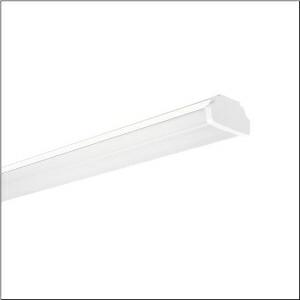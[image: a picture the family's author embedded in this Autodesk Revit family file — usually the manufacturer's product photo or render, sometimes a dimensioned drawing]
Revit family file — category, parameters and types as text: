
# Revit family: modario_r__31_ho_53bm811m1v4120_5d14
name_source: partatom
category: Lighting Fixtures
units: mm (PartAtom-declared; Revit-internal decimal feet)

## family parameters
Cut with Voids When Loaded = No
Host = Face
Light Source = No
Part Type = Normal
Room Calculation Point = No
Round Connector Dimension = Use Diameter
Shared = No

## types (1)
- --- (1 x LED, 12380 lm, 77.3 W, 4000K)
    Apparent Load = 77 VA
    CIE Flux Codes = 52 78 94 90 100
    Color Rendering = 80
    Color Temperature = 4000K
    Default Elevation = 1800 mm
    Description = Modario® 31 HO, luminaire insert, of sheet steel, coil coated, white, length: 1.495mm, width: 81mm, height: 82mm, LED rated luminous flux: 12.380lm, light colour: 840, control gear: ON/OFF Multilumen, control gear: ECG Multilumen, with plug, 3-pole, with phase selection, mains connection: 220..240V, AC, 50/60Hz, primary optical cover: cover, of PMMA, light emission: direct distribution, primary light characteristic: symmetric, protection rating (complete): IP20, protection rating (LED compartment): IP50, insulation class (complete): insulation class I (protective earthing), certification: CE, ENEC, VDE, UKCA, permissible ambient temperature for indoor applications: -35..+35°C, corresponds to IFS (International Featured Standards) requirements for safety and quality in the food industry, reducing of maximum allowable ambient temperature of 5°C with ceiling mounting, packaging unit: 1 piece
    Height = 92 mm
    Lamp = 1 x LED
    Lamp Light Flux = 12380 lm
    Lamp Power = 77.3 W
    Lamp count = 1
    Length = 1495 mm
    Luminous efficacy = 160 lm/W
    Manufacturer = Siteco
    ModVariant = No
    Model = 53BM811M1V4120
    Mounting Place = Ceiling
    Mounting Type = Pendant
    Number of Poles = 1
    OnlyDefault = Yes
    Power Factor = 1
    Product Name = Modario® 31 HO
    Product group = luminaire insert
    ProductGroupID = 902
    Protection Class = Protection class I
    Protection Degree = IP 20
    RLX_Detail_Level = 1
    RlxData = <blob elided: 40045 chars, md5=07634e21>
    Socket = socket
    Standby Power = 0 W
    System Light Flux = 12380 lm
    System Power = 77 W
    Type Comments = factory setting: luminous flux: 100 % | (A | C | E) | 173 mA
    Type Image = l_1003447.jpg
    URL = http://relux.com
    VarID = @adj_125385
    Voltage = 0 V
    Weight = 0.00 kg
    Width = 81 mm

## geometry (parser evidence)
native form markers: Blend x4, Sweep x11
no freeform markers — native parametric forms only
